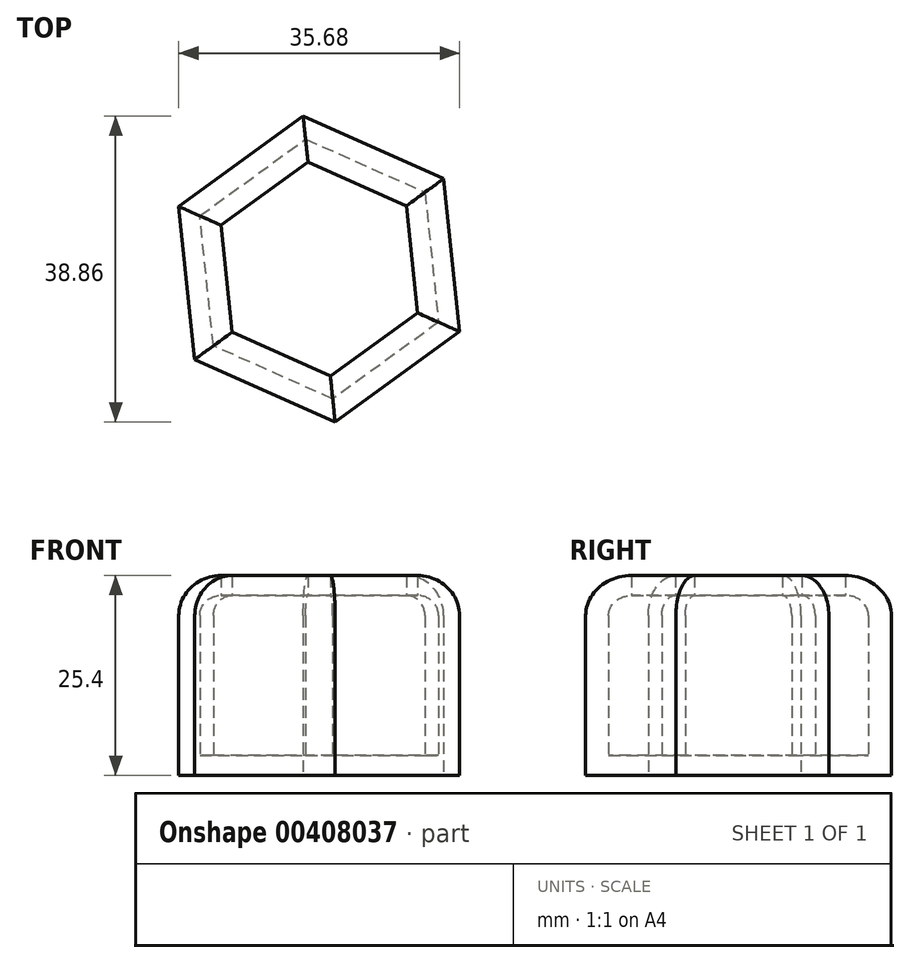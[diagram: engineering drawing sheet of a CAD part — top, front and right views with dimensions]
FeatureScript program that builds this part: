
annotation { "Feature Type Name" : "Feature", "Feature Type Description" : "" }
export const myFeature = defineFeature(function(context is Context, id is Id, definition is map)
    precondition{}
    {
        {
            var Q0;
            Q0=qCreatedBy(makeId("Top.planeOp"),FACE);
            var sketch = newSketch(context, id + "F0", { "sketchPlane" : qUnion([Q0])});
            skCircle(sketch, "E0.cCircle", {"center": v(-27.12, 29.8) * mm, "radius": 16.92 * mm, "construction": true});
            skLineSegment(sketch, "E0.0", {"start": v(-9.28, 21.84) * mm, "end": v(-25.09, 10.37) * mm});
            skLineSegment(sketch, "E0.1", {"start": v(-25.09, 10.37) * mm, "end": v(-42.93, 18.33) * mm});
            skLineSegment(sketch, "E0.2", {"start": v(-42.93, 18.33) * mm, "end": v(-44.96, 37.76) * mm});
            skLineSegment(sketch, "E0.3", {"start": v(-44.96, 37.76) * mm, "end": v(-29.15, 49.23) * mm});
            skLineSegment(sketch, "E0.4", {"start": v(-29.15, 49.23) * mm, "end": v(-11.3, 41.27) * mm});
            skLineSegment(sketch, "E0.5", {"start": v(-11.3, 41.27) * mm, "end": v(-9.28, 21.84) * mm});
            skPoint(sketch, "E0.0.midPoint", {"position": v(-17.18, 16.1) * mm});
            skSolve(sketch);
        }
        {
            var Q0;
            Q0=makeQuery(id+"F0.imprint","IMPRINT",FACE,{"disambiguationData":[TD([[makeQuery(id+"F0.imprint","IMPRINT",EDGE,{"derivedFrom":sQuery(id+"F0.wireOp",EDGE,"E0.0")}),-1.0]])]});
            extrude(context, id + "F1", {"entities" : qUnion([Q0]), "depth" : 25.4 * mm});
        }
        {
            var Q0;
            Q0=makeQuery(id+"F1.opExtrude","CAP_EDGE",EDGE,{"disambiguationData":[OSD([sQuery(id+"F0.wireOp",EDGE,"E0.3")])],"isStart":false});
            var Q1;
            Q1=makeQuery(id+"F1.opExtrude","CAP_EDGE",EDGE,{"disambiguationData":[OSD([sQuery(id+"F0.wireOp",EDGE,"E0.4")])],"isStart":false});
            var Q2;
            Q2=makeQuery(id+"F1.opExtrude","CAP_EDGE",EDGE,{"disambiguationData":[OSD([sQuery(id+"F0.wireOp",EDGE,"E0.5")])],"isStart":false});
            var Q3;
            Q3=makeQuery(id+"F1.opExtrude","CAP_EDGE",EDGE,{"disambiguationData":[OSD([sQuery(id+"F0.wireOp",EDGE,"E0.0")])],"isStart":false});
            var Q4;
            Q4=makeQuery(id+"F1.opExtrude","CAP_EDGE",EDGE,{"disambiguationData":[OSD([sQuery(id+"F0.wireOp",EDGE,"E0.1")])],"isStart":false});
            var Q5;
            Q5=makeQuery(id+"F1.opExtrude","CAP_FACE",FACE,{"disambiguationData":[OSD([sQuery(id+"F0.wireOp",EDGE,"E0.0"),sQuery(id+"F0.wireOp",EDGE,"E0.1"),sQuery(id+"F0.wireOp",EDGE,"E0.2"),sQuery(id+"F0.wireOp",EDGE,"E0.3"),sQuery(id+"F0.wireOp",EDGE,"E0.4"),sQuery(id+"F0.wireOp",EDGE,"E0.5")])],"isStart":false});
            fillet(context, id + "F2", {"entities" : qUnion([Q0, Q1, Q2, Q3, Q4, Q5]), "radius" : 5.08 * mm, "tangentPropagation" : true, "allowEdgeOverflow" : false});
        }
        {
            var Q0;
            Q0=makeQuery(id+"F1.opExtrude","CAP_FACE",FACE,{"disambiguationData":[OSD([sQuery(id+"F0.wireOp",EDGE,"E0.0"),sQuery(id+"F0.wireOp",EDGE,"E0.1"),sQuery(id+"F0.wireOp",EDGE,"E0.2"),sQuery(id+"F0.wireOp",EDGE,"E0.3"),sQuery(id+"F0.wireOp",EDGE,"E0.4"),sQuery(id+"F0.wireOp",EDGE,"E0.5")])],"isStart":false});
            shell(context, id + "F3", {"entities" : qUnion([Q0]), "thickness" : 2.54 * mm});
        }
    });
